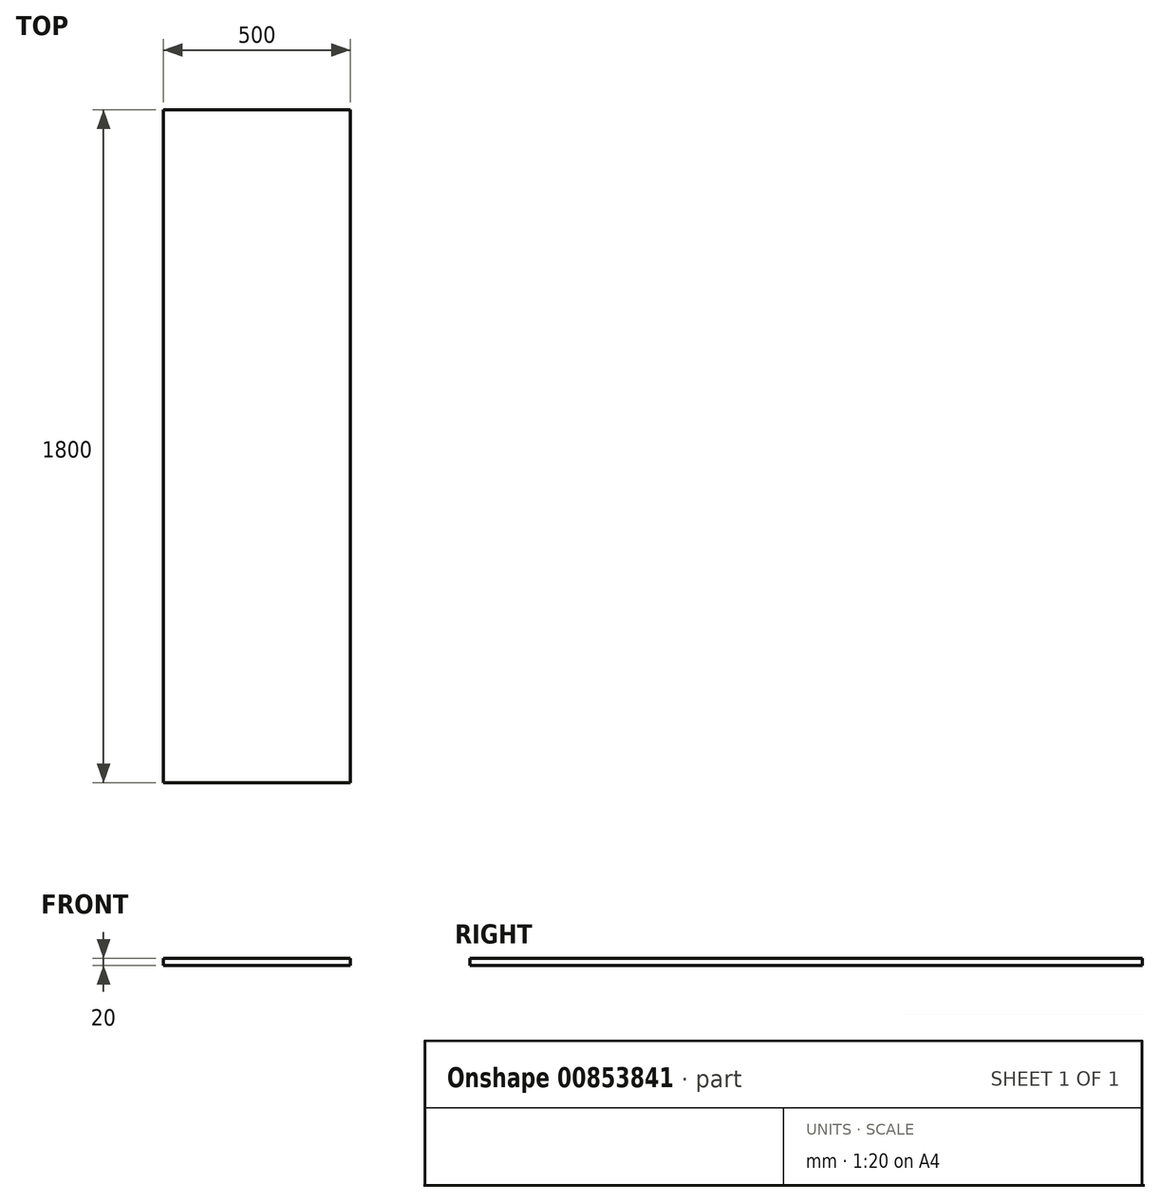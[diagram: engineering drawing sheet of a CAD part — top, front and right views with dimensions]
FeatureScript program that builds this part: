
annotation { "Feature Type Name" : "Feature", "Feature Type Description" : "" }
export const myFeature = defineFeature(function(context is Context, id is Id, definition is map)
    precondition{}
    {
        {
            var Q0;
            Q0=qCreatedBy(makeId("Front.planeOp"),FACE);
            var sketch = newSketch(context, id + "F0", { "sketchPlane" : qUnion([Q0])});
            skLineSegment(sketch, "E0.bottom", {"start": v(-250, 0) * mm, "end": v(250, 0) * mm});
            skLineSegment(sketch, "E0.top", {"start": v(-250, 20) * mm, "end": v(250, 20) * mm});
            skLineSegment(sketch, "E0.left", {"start": v(-250, 0) * mm, "end": v(-250, 20) * mm});
            skLineSegment(sketch, "E0.right", {"start": v(250, 0) * mm, "end": v(250, 20) * mm});
            skSolve(sketch);
        }
        {
            var Q0;
            Q0 = qSketchRegion(id + "F0", true);
            extrude(context, id + "F1", {"entities" : qUnion([Q0]), "oppositeDirection" : true, "depth" : 1800 * mm, "offsetDistance" : 25 * mm});
        }
    });
